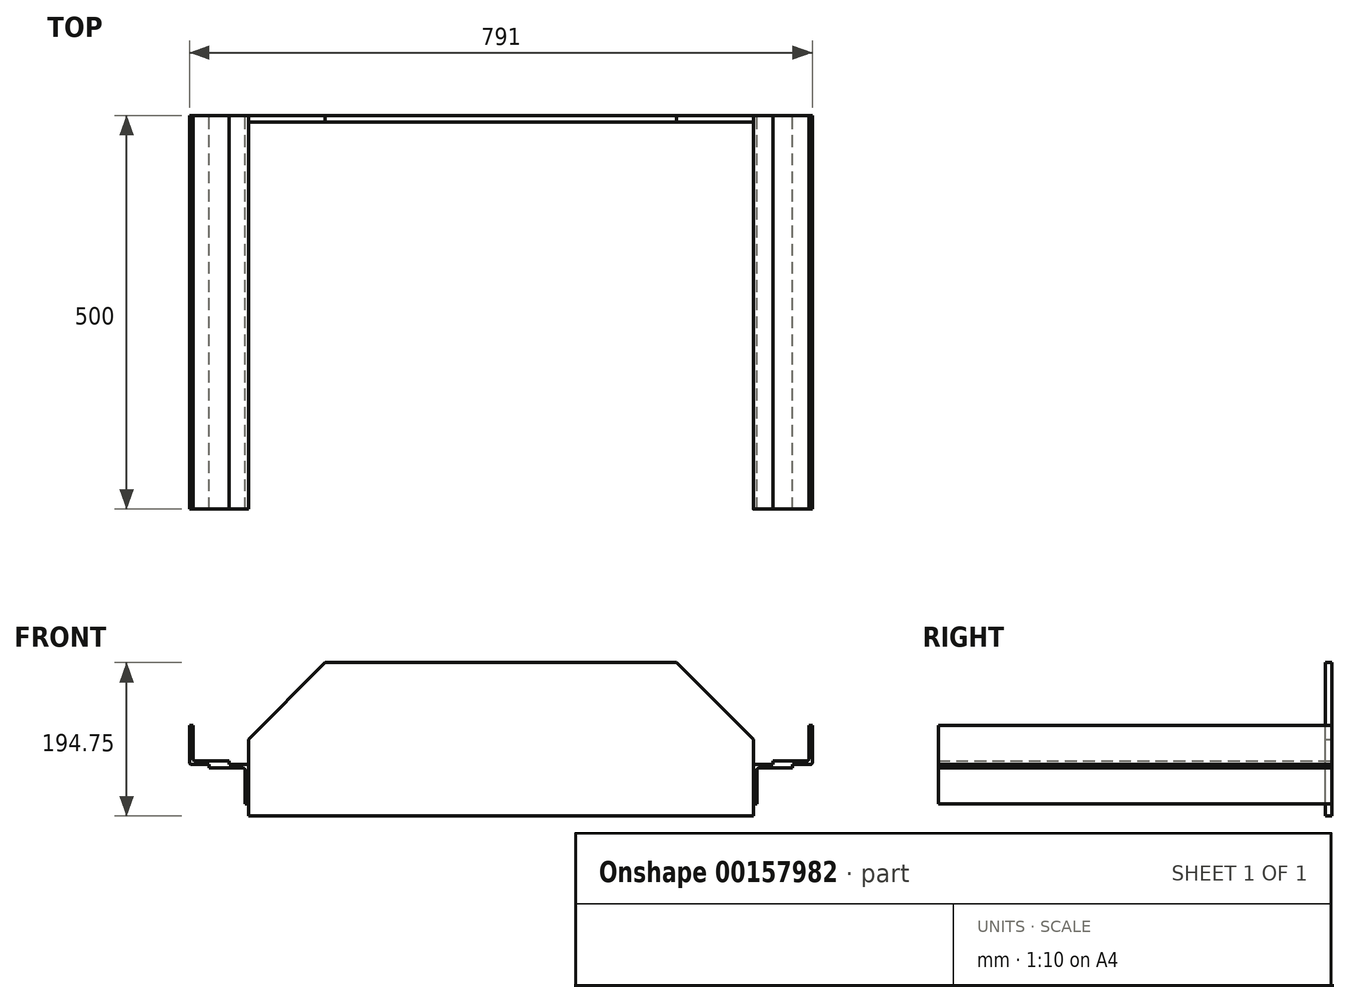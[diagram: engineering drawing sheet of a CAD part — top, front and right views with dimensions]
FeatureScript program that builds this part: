
annotation { "Feature Type Name" : "Feature", "Feature Type Description" : "" }
export const myFeature = defineFeature(function(context is Context, id is Id, definition is map)
    precondition{}
    {
        {
            var Q0;
            Q0=qCreatedBy(makeId("Front.planeOp"),FACE);
            var sketch = newSketch(context, id + "F0", { "sketchPlane" : qUnion([Q0])});
            skLineSegment(sketch, "E0", {"start": v(0, 2.5) * mm, "end": v(0, 50) * mm});
            skLineSegment(sketch, "E1", {"start": v(0, 50) * mm, "end": v(4.5, 50) * mm});
            skLineSegment(sketch, "E2", {"start": v(4.5, 50) * mm, "end": v(4.5, 7) * mm});
            skLineSegment(sketch, "E3", {"start": v(7, 4.5) * mm, "end": v(50, 4.5) * mm});
            skLineSegment(sketch, "E4", {"start": v(50, 4.5) * mm, "end": v(50, 0) * mm});
            skLineSegment(sketch, "E5", {"start": v(50, 0) * mm, "end": v(2.5, 0) * mm});
            skPoint(sketch, "E6.visualSharp", {"position": v(4.5, 4.5) * mm});
            skArc(sketch, "E6.filletArc", {"start": v(4.5, 7) * mm, "mid": v(5.23, 5.23) * mm, "end": v(7, 4.5) * mm});
            skPoint(sketch, "E7.visualSharp", {"position": v(0, 0) * mm});
            skArc(sketch, "E7.filletArc", {"start": v(0, 2.5) * mm, "mid": v(0.73, 0.73) * mm, "end": v(2.5, 0) * mm});
            skLineSegment(sketch, "E8.0", {"start": v(395.5, 97.82) * mm, "end": v(395.5, -90.94) * mm, "construction": true});
            skArc(sketch, "E9.MirrorCS", {"start": v(786.5, 7) * mm, "mid": v(785.77, 5.23) * mm, "end": v(784, 4.5) * mm});
            skArc(sketch, "E10.MirrorCS", {"start": v(791, 2.5) * mm, "mid": v(790.27, 0.73) * mm, "end": v(788.5, 0) * mm});
            skLineSegment(sketch, "E11.MirrorCS", {"start": v(791, 50) * mm, "end": v(786.5, 50) * mm});
            skLineSegment(sketch, "E12.MirrorCS", {"start": v(741, 4.5) * mm, "end": v(741, 0) * mm});
            skPoint(sketch, "E13.MirrorP", {"position": v(786.5, 4.5) * mm});
            skPoint(sketch, "E14.MirrorP", {"position": v(791, 0) * mm});
            skLineSegment(sketch, "E15.MirrorCS", {"start": v(786.5, 50) * mm, "end": v(786.5, 7) * mm});
            skLineSegment(sketch, "E16.MirrorCS", {"start": v(784, 4.5) * mm, "end": v(741, 4.5) * mm});
            skLineSegment(sketch, "E17.MirrorCS", {"start": v(791, 2.5) * mm, "end": v(791, 50) * mm});
            skLineSegment(sketch, "E18.MirrorCS", {"start": v(741, 0) * mm, "end": v(788.5, 0) * mm});
            skLineSegment(sketch, "E19", {"start": v(25, 0) * mm, "end": v(72.5, 0) * mm});
            skLineSegment(sketch, "E20", {"start": v(75, -2.5) * mm, "end": v(75, -50) * mm});
            skLineSegment(sketch, "E21", {"start": v(75, -50) * mm, "end": v(70.5, -50) * mm});
            skLineSegment(sketch, "E22", {"start": v(70.5, -50) * mm, "end": v(70.5, -7) * mm});
            skLineSegment(sketch, "E23", {"start": v(68, -4.5) * mm, "end": v(25, -4.5) * mm});
            skLineSegment(sketch, "E24", {"start": v(25, -4.5) * mm, "end": v(25, 0) * mm});
            skPoint(sketch, "E25.visualSharp", {"position": v(70.5, -4.5) * mm});
            skArc(sketch, "E25.filletArc", {"start": v(70.5, -7) * mm, "mid": v(69.77, -5.23) * mm, "end": v(68, -4.5) * mm});
            skPoint(sketch, "E26.visualSharp", {"position": v(75, 0) * mm});
            skArc(sketch, "E26.filletArc", {"start": v(75, -2.5) * mm, "mid": v(74.27, -0.73) * mm, "end": v(72.5, 0) * mm});
            skLineSegment(sketch, "E27.MirrorCS", {"start": v(766, 0) * mm, "end": v(718.5, 0) * mm});
            skLineSegment(sketch, "E28.MirrorCS", {"start": v(723, -4.5) * mm, "end": v(766, -4.5) * mm});
            skLineSegment(sketch, "E29.MirrorCS", {"start": v(766, -4.5) * mm, "end": v(766, 0) * mm});
            skArc(sketch, "E30.MirrorCS", {"start": v(716, -2.5) * mm, "mid": v(716.73, -0.73) * mm, "end": v(718.5, 0) * mm});
            skLineSegment(sketch, "E31.MirrorCS", {"start": v(716, -50) * mm, "end": v(720.5, -50) * mm});
            skArc(sketch, "E32.MirrorCS", {"start": v(720.5, -7) * mm, "mid": v(721.23, -5.23) * mm, "end": v(723, -4.5) * mm});
            skPoint(sketch, "E33.MirrorP", {"position": v(716, 0) * mm});
            skLineSegment(sketch, "E34.MirrorCS", {"start": v(716, -2.5) * mm, "end": v(716, -50) * mm});
            skLineSegment(sketch, "E35.MirrorCS", {"start": v(720.5, -50) * mm, "end": v(720.5, -7) * mm});
            skPoint(sketch, "E36.MirrorP", {"position": v(720.5, -4.5) * mm});
            skSolve(sketch);
        }
        {
            var Q0;
            Q0 = qSketchRegion(id + "F0", true);
            extrude(context, id + "F1", {"entities" : qUnion([Q0]), "endBound" : BoundingType.SYMMETRIC, "depth" : 500 * mm});
        }
        {
            var Q0;
            Q0=qCreatedBy(makeId("Front.planeOp"),FACE);
            cPlane(context, id + "F2", {"entities" : qUnion([Q0]), "cplaneType" : CPlaneType.OFFSET, "offset" : 250 * mm, "oppositeDirection" : true, "width" : 150 * mm, "height" : 150 * mm});
        }
        {
            var Q0;
            Q0=qCreatedBy(id+"F2.planeOp",FACE);
            var sketch = newSketch(context, id + "F3", { "sketchPlane" : qUnion([Q0])});
            skLineSegment(sketch, "E37.bottom", {"start": v(75, -65.25) * mm, "end": v(716, -65.25) * mm});
            skLineSegment(sketch, "E37.top", {"start": v(172.38, 129.5) * mm, "end": v(618.62, 129.5) * mm});
            skLineSegment(sketch, "E37.left", {"start": v(75, -65.25) * mm, "end": v(75, 32.12) * mm});
            skLineSegment(sketch, "E37.right", {"start": v(716, -65.25) * mm, "end": v(716, 32.12) * mm});
            skLineSegment(sketch, "E38", {"start": v(716, 32.12) * mm, "end": v(618.62, 129.5) * mm});
            skLineSegment(sketch, "E39", {"start": v(75, 32.12) * mm, "end": v(172.38, 129.5) * mm});
            skPoint(sketch, "E40.orphan", {"position": v(716, 129.5) * mm});
            skPoint(sketch, "E41.orphan", {"position": v(75, 129.5) * mm});
            skSolve(sketch);
        }
        {
            var Q0;
            Q0 = qSketchRegion(id + "F3", true);
            extrude(context, id + "F4", {"entities" : qUnion([Q0]), "depth" : 8 * mm});
        }
    });
